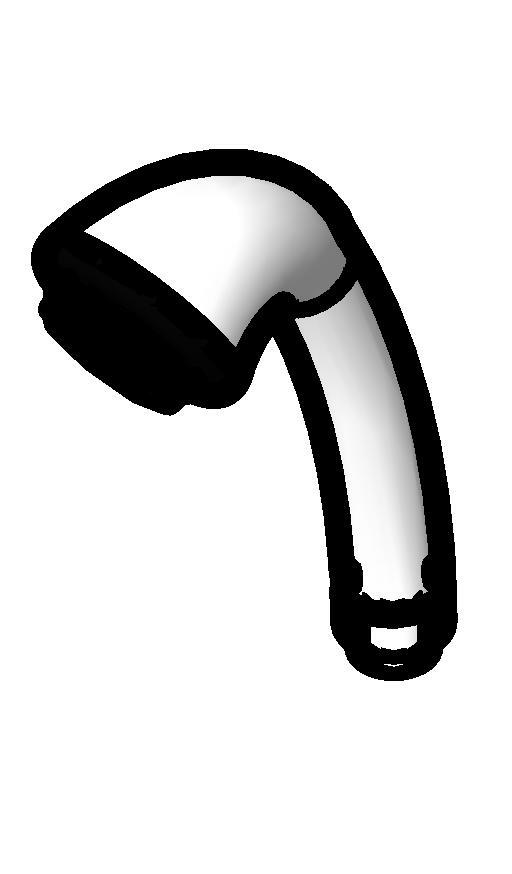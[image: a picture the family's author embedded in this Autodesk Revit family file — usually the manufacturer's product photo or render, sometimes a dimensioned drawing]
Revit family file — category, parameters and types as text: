
# Revit family: Deca_Ducha Manual Quadrada_4806.C.QUA
name_source: partatom
category: Plumbing Fixtures
revit_build: Autodesk Revit Architecture 2012 (Build: 20120126_0600(x64)
units: mm (PartAtom-declared; Revit-internal decimal feet)

## types (1)
- 4806.C.QUA_Cromado CR10
    Aprovado por = Contino/quattroD
    Assembly Code = D2010700
    Atendimento ao Cliente = 0800-0117073
    Consumo = Varia com a pressão (consultar catálogo)
    Criado por = Contino/quattroD
    Código = 4806.C.QUA
    Default Elevation = 2000 mm  [stored 6.56168 ft]
    Description = Ducha  manual
    Diâmetro Ponto de Agua = 15 mm  [stored 0.0492126 ft]
    Ducha Manual = Deca CR10 Cromado Metal
    Flow Pressure = 0.00 psi
    HWFU = 0
    Informações Complementares = Recomendável com pressão mínima de 4 m.c.a para aquecedor de passagem e de 2 m.c.a. para aquecedor de acumulação
    Linha = Quadrada
    Louça/Metais = Metal
    Manufacturer = Deca
    Material = Deca_Latão Cromado e Plástico de Engenharia
    Model = 4806.C.QUA
    Norma = ABNT NBR 15206:2005
    Peso Liquido (Kg) = 0.21
    Pressão = 2 a 40 mca
    Produto = Ducha manual Quadrada
    Raio Ponto de Agua = 8 mm  [stored 0.0262467 ft]
    Segmento = Luxo
    URL = www.deca.com.br/produtos
    Variações de COR = Cromado (4806.C.QUA)
    WFU = 0

note: [stored X ft] marks values corroborated as IEEE doubles in the binary element streams (Revit-internal decimal feet)

## geometry (parser evidence)
native form markers: Blend x4, Sweep x3
no freeform markers — native parametric forms only
